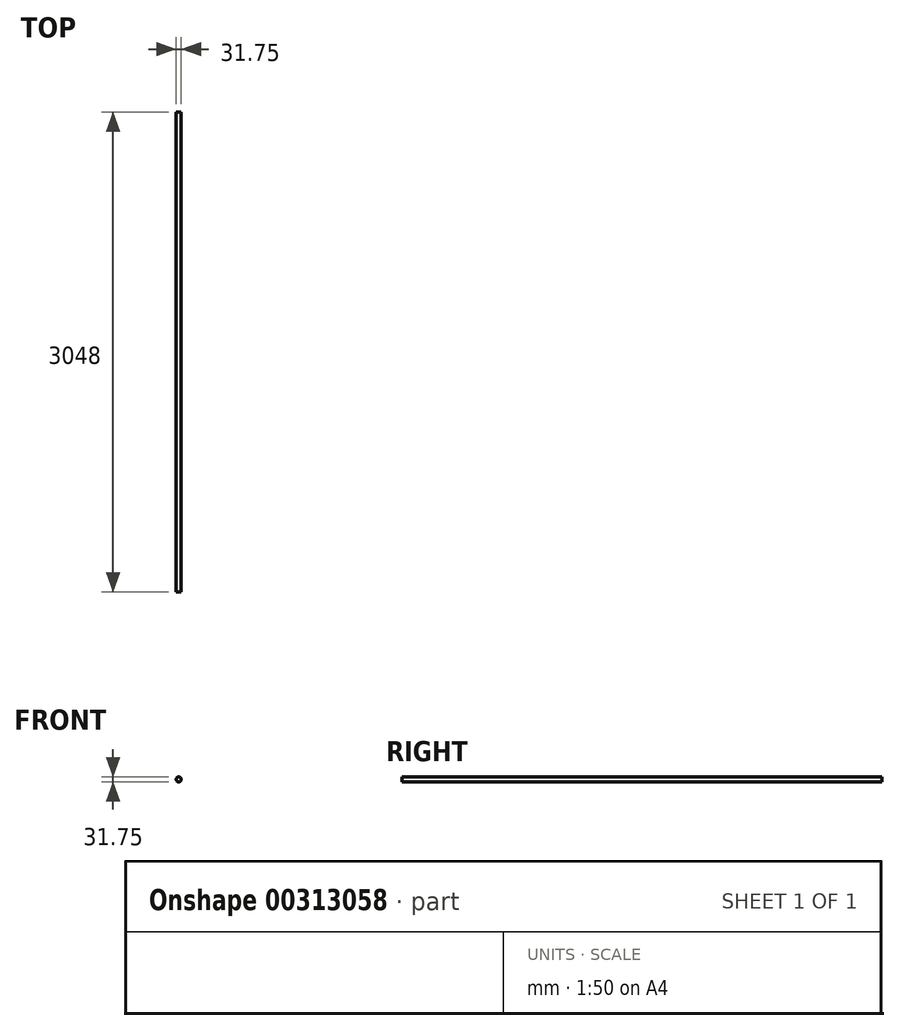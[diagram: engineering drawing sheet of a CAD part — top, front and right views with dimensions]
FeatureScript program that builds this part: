
annotation { "Feature Type Name" : "Feature", "Feature Type Description" : "" }
export const myFeature = defineFeature(function(context is Context, id is Id, definition is map)
    precondition{}
    {
        {
            var Q0;
            Q0=qCreatedBy(makeId("Front.planeOp"),FACE);
            var sketch = newSketch(context, id + "F0", { "sketchPlane" : qUnion([Q0])});
            skCircle(sketch, "E0", {"center": v(-30.8, 29.24) * mm, "radius": 15.88 * mm});
            skSolve(sketch);
        }
        {
            var Q0;
            Q0 = qSketchRegion(id + "F0", true);
            extrude(context, id + "F1", {"entities" : qUnion([Q0]), "depth" : 3048 * mm});
        }
    });
